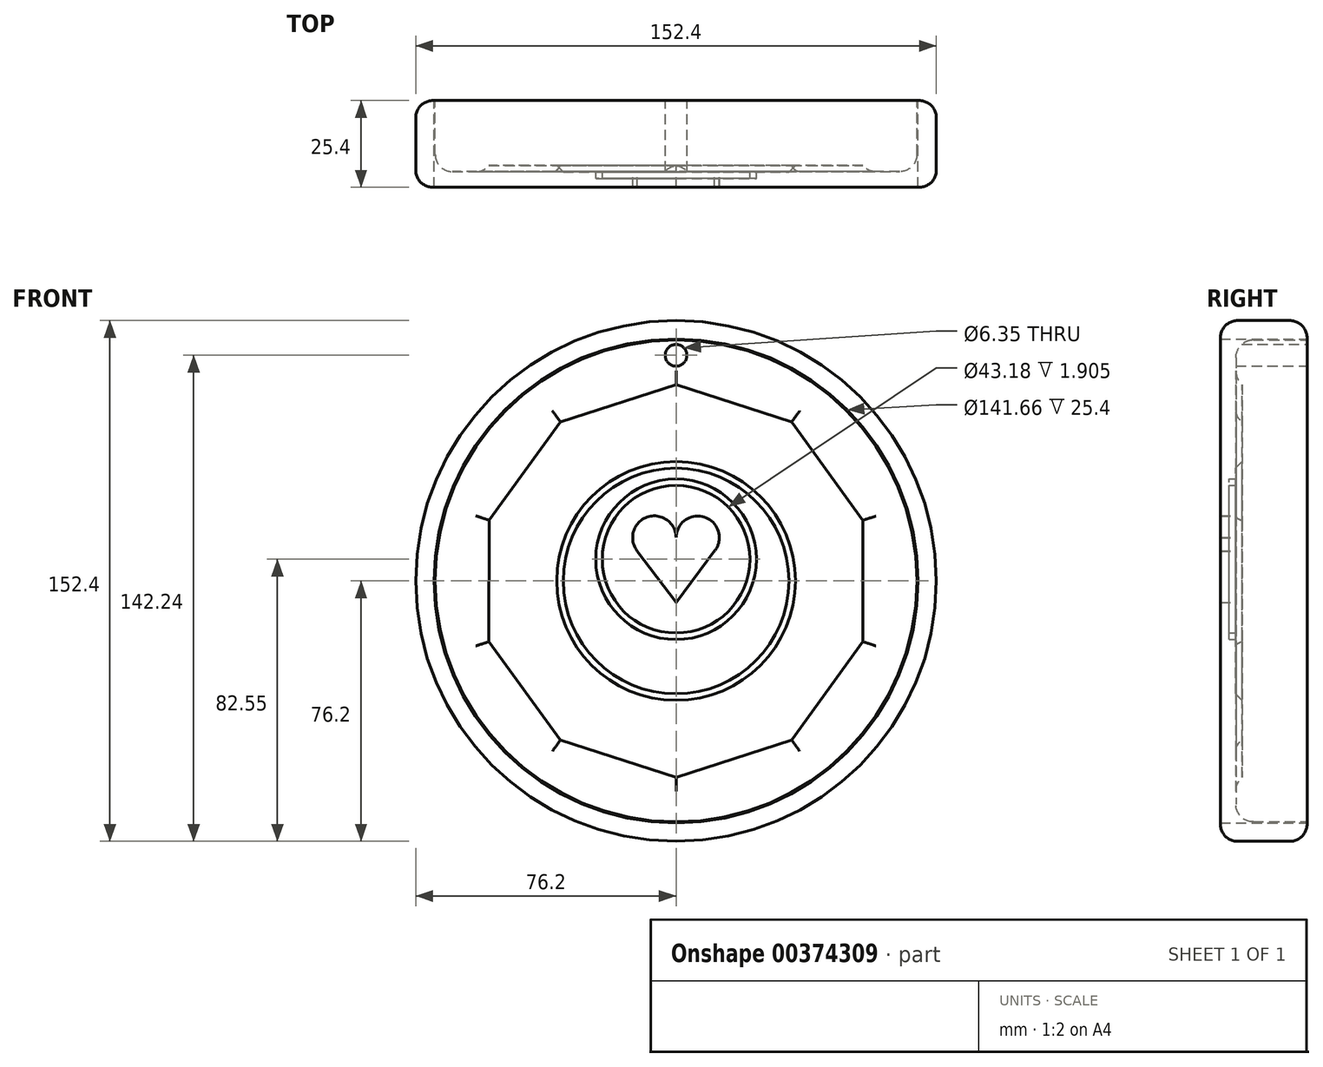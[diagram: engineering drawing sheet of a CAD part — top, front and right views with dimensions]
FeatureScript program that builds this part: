
annotation { "Feature Type Name" : "Feature", "Feature Type Description" : "" }
export const myFeature = defineFeature(function(context is Context, id is Id, definition is map)
    precondition{}
    {
        {
            var Q0;
            Q0=qCreatedBy(makeId("Front.planeOp"),FACE);
            var sketch = newSketch(context, id + "F0", { "sketchPlane" : qUnion([Q0])});
            skCircle(sketch, "E0", {"center": v(0, 0) * mm, "radius": 76.2 * mm});
            skPoint(sketch, "E1.0.midPoint", {"position": v(59.75, 28.13) * mm});
            skCircle(sketch, "E2", {"center": v(0, 0) * mm, "radius": 70.83 * mm});
            skSolve(sketch);
        }
        {
            var Q0;
            {var subQ0=sQuery(id+"F0.wireOp",EDGE,"E1.5");var subQ1=sQuery(id+"F0.wireOp",EDGE,"E0");var subQ2=makeQuery(id+"F0.imprint","INTERSECT",VERTEX,{"disambiguationData":[OD(0.0)],"derivedFrom":[subQ1,subQ0]});Q0=makeQuery(id+"F0.imprint","IMPRINT",FACE,{"disambiguationData":[TD([[makeQuery(id+"F0.imprint","IMPRINT",EDGE,{"disambiguationData":[TD([[subQ2,1.0]])],"derivedFrom":subQ1}),-1.0]])]});}
            var Q1;
            {var subQ0=sQuery(id+"F0.wireOp",EDGE,"E1.5");var subQ1=sQuery(id+"F0.wireOp",EDGE,"E0");var subQ2=makeQuery(id+"F0.imprint","INTERSECT",VERTEX,{"disambiguationData":[OD(1.0)],"derivedFrom":[subQ1,subQ0]});Q1=makeQuery(id+"F0.imprint","IMPRINT",FACE,{"disambiguationData":[TD([[makeQuery(id+"F0.imprint","IMPRINT",EDGE,{"disambiguationData":[TD([[subQ2,-1.0]])],"derivedFrom":subQ1}),-1.0]])]});}
            var Q2;
            {var subQ0=sQuery(id+"F0.wireOp",EDGE,"E1.4");var subQ1=sQuery(id+"F0.wireOp",EDGE,"E0");var subQ2=makeQuery(id+"F0.imprint","INTERSECT",VERTEX,{"disambiguationData":[OD(1.0)],"derivedFrom":[subQ1,subQ0]});Q2=makeQuery(id+"F0.imprint","IMPRINT",FACE,{"disambiguationData":[TD([[makeQuery(id+"F0.imprint","IMPRINT",EDGE,{"disambiguationData":[TD([[subQ2,-1.0]])],"derivedFrom":subQ1}),-1.0]])]});}
            var Q3;
            {var subQ0=sQuery(id+"F0.wireOp",EDGE,"E1.3");var subQ1=sQuery(id+"F0.wireOp",EDGE,"E0");var subQ2=makeQuery(id+"F0.imprint","INTERSECT",VERTEX,{"disambiguationData":[OD(1.0)],"derivedFrom":[subQ1,subQ0]});Q3=makeQuery(id+"F0.imprint","IMPRINT",FACE,{"disambiguationData":[TD([[makeQuery(id+"F0.imprint","IMPRINT",EDGE,{"disambiguationData":[TD([[subQ2,-1.0]])],"derivedFrom":subQ1}),-1.0]])]});}
            var Q4;
            {var subQ0=sQuery(id+"F0.wireOp",EDGE,"E1.2");var subQ1=sQuery(id+"F0.wireOp",EDGE,"E0");var subQ2=makeQuery(id+"F0.imprint","INTERSECT",VERTEX,{"disambiguationData":[OD(1.0)],"derivedFrom":[subQ1,subQ0]});Q4=makeQuery(id+"F0.imprint","IMPRINT",FACE,{"disambiguationData":[TD([[makeQuery(id+"F0.imprint","IMPRINT",EDGE,{"disambiguationData":[TD([[subQ2,-1.0]])],"derivedFrom":subQ1}),-1.0]])]});}
            var Q5;
            {var subQ0=sQuery(id+"F0.wireOp",EDGE,"E1.1");var subQ1=sQuery(id+"F0.wireOp",EDGE,"E0");var subQ2=makeQuery(id+"F0.imprint","INTERSECT",VERTEX,{"disambiguationData":[OD(1.0)],"derivedFrom":[subQ1,subQ0]});Q5=makeQuery(id+"F0.imprint","IMPRINT",FACE,{"disambiguationData":[TD([[makeQuery(id+"F0.imprint","IMPRINT",EDGE,{"disambiguationData":[TD([[subQ2,-1.0]])],"derivedFrom":subQ1}),-1.0]])]});}
            var Q6;
            {var subQ0=sQuery(id+"F0.wireOp",EDGE,"E1.5");var subQ1=sQuery(id+"F0.wireOp",EDGE,"E0");var subQ2=makeQuery(id+"F0.imprint","INTERSECT",VERTEX,{"disambiguationData":[OD(0.0)],"derivedFrom":[subQ1,subQ0]});Q6=makeQuery(id+"F0.imprint","IMPRINT",FACE,{"disambiguationData":[TD([[makeQuery(id+"F0.imprint","IMPRINT",EDGE,{"disambiguationData":[TD([[subQ2,-1.0]])],"derivedFrom":subQ1}),1.0]])]});}
            var Q7;
            {var subQ0=sQuery(id+"F0.wireOp",EDGE,"E1.4");var subQ1=sQuery(id+"F0.wireOp",EDGE,"E0");var subQ2=makeQuery(id+"F0.imprint","INTERSECT",VERTEX,{"disambiguationData":[OD(0.0)],"derivedFrom":[subQ1,subQ0]});Q7=makeQuery(id+"F0.imprint","IMPRINT",FACE,{"disambiguationData":[TD([[makeQuery(id+"F0.imprint","IMPRINT",EDGE,{"disambiguationData":[TD([[subQ2,-1.0]])],"derivedFrom":subQ1}),1.0]])]});}
            var Q8;
            {var subQ0=sQuery(id+"F0.wireOp",EDGE,"E1.3");var subQ1=sQuery(id+"F0.wireOp",EDGE,"E0");var subQ7=makeQuery(id+"F0.imprint","INTERSECT",VERTEX,{"disambiguationData":[OD(0.0)],"derivedFrom":[subQ1,subQ0]});Q8=makeQuery(id+"F0.imprint","IMPRINT",FACE,{"disambiguationData":[TD([[makeQuery(id+"F0.imprint","IMPRINT",EDGE,{"disambiguationData":[TD([[subQ7,-1.0]])],"derivedFrom":subQ1}),1.0]])]});}
            var Q9;
            {var subQ0=sQuery(id+"F0.wireOp",EDGE,"E1.2");var subQ1=sQuery(id+"F0.wireOp",EDGE,"E0");var subQ2=makeQuery(id+"F0.imprint","INTERSECT",VERTEX,{"disambiguationData":[OD(0.0)],"derivedFrom":[subQ1,subQ0]});Q9=makeQuery(id+"F0.imprint","IMPRINT",FACE,{"disambiguationData":[TD([[makeQuery(id+"F0.imprint","IMPRINT",EDGE,{"disambiguationData":[TD([[subQ2,-1.0]])],"derivedFrom":subQ1}),1.0]])]});}
            var Q10;
            {var subQ0=sQuery(id+"F0.wireOp",EDGE,"E1.1");var subQ1=sQuery(id+"F0.wireOp",EDGE,"E0");var subQ2=makeQuery(id+"F0.imprint","INTERSECT",VERTEX,{"disambiguationData":[OD(0.0)],"derivedFrom":[subQ1,subQ0]});Q10=makeQuery(id+"F0.imprint","IMPRINT",FACE,{"disambiguationData":[TD([[makeQuery(id+"F0.imprint","IMPRINT",EDGE,{"disambiguationData":[TD([[subQ2,-1.0]])],"derivedFrom":subQ1}),1.0]])]});}
            var Q11;
            {var subQ3=sQuery(id+"F0.wireOp",EDGE,"E1.0");var subQ5=sQuery(id+"F0.wireOp",EDGE,"E0");var subQ8=makeQuery(id+"F0.imprint","INTERSECT",VERTEX,{"disambiguationData":[OD(0.0)],"derivedFrom":[subQ5,subQ3]});Q11=makeQuery(id+"F0.imprint","IMPRINT",FACE,{"disambiguationData":[TD([[makeQuery(id+"F0.imprint","IMPRINT",EDGE,{"disambiguationData":[TD([[subQ8,1.0]])],"derivedFrom":subQ5}),1.0]])]});}
            var Q12;
            Q12=makeQuery(id+"F0.imprint","IMPRINT",FACE,{"disambiguationData":[TD([[makeQuery(id+"F0.imprint","IMPRINT",EDGE,{"derivedFrom":sQuery(id+"F0.wireOp",EDGE,"E0")}),1.0]])]});
            extrude(context, id + "F1", {"entities" : qUnion([Q0, Q1, Q2, Q3, Q4, Q5, Q6, Q7, Q8, Q9, Q10, Q11, Q12]), "depth" : 25.4 * mm});
        }
        {
            var Q0;
            Q0=makeQuery(id+"F1.opExtrude","SWEPT_FACE",FACE,{"disambiguationData":[OSD([sQuery(id+"F0.wireOp",EDGE,"E0")])]});
            fillet(context, id + "F2", {"entities" : qUnion([Q0]), "radius" : 5.08 * mm, "tangentPropagation" : true, "allowEdgeOverflow" : false});
        }
        {
            var Q0;
            Q0=qCreatedBy(makeId("Front.planeOp"),FACE);
            var sketch = newSketch(context, id + "F3", { "sketchPlane" : qUnion([Q0])});
            skCircle(sketch, "E3", {"center": v(0, 0) * mm, "radius": 70.5 * mm});
            skLineSegment(sketch, "E4.0", {"start": v(54.68, 17.76) * mm, "end": v(54.68, -17.76) * mm});
            skLineSegment(sketch, "E4.1", {"start": v(54.68, -17.76) * mm, "end": v(33.8, -46.52) * mm});
            skLineSegment(sketch, "E4.2", {"start": v(33.8, -46.52) * mm, "end": v(0, -57.49) * mm});
            skLineSegment(sketch, "E4.3", {"start": v(0, -57.49) * mm, "end": v(-33.8, -46.52) * mm});
            skLineSegment(sketch, "E4.4", {"start": v(-33.8, -46.52) * mm, "end": v(-54.8, -17.79) * mm});
            skLineSegment(sketch, "E4.5", {"start": v(-54.8, -17.79) * mm, "end": v(-54.72, 17.79) * mm});
            skLineSegment(sketch, "E4.6", {"start": v(-54.72, 17.79) * mm, "end": v(-33.85, 46.55) * mm});
            skLineSegment(sketch, "E4.7", {"start": v(-33.85, 46.55) * mm, "end": v(0, 57.49) * mm});
            skLineSegment(sketch, "E4.8", {"start": v(0, 57.49) * mm, "end": v(33.8, 46.52) * mm});
            skLineSegment(sketch, "E4.9", {"start": v(33.8, 46.52) * mm, "end": v(54.68, 17.76) * mm});
            skPoint(sketch, "E4.0.midPoint", {"position": v(54.68, 0) * mm});
            skLineSegment(sketch, "E5", {"start": v(33.8, 46.52) * mm, "end": v(41.99, 56.62) * mm});
            skLineSegment(sketch, "E6", {"start": v(54.68, 17.76) * mm, "end": v(67.2, 21.26) * mm});
            skLineSegment(sketch, "E7", {"start": v(54.68, -17.76) * mm, "end": v(66.93, -22.12) * mm});
            skLineSegment(sketch, "E8", {"start": v(33.8, -46.52) * mm, "end": v(41.86, -56.72) * mm});
            skLineSegment(sketch, "E9", {"start": v(0, -57.49) * mm, "end": v(0, -70.5) * mm});
            skLineSegment(sketch, "E10", {"start": v(0, 57.49) * mm, "end": v(0, 70.5) * mm});
            skLineSegment(sketch, "E11", {"start": v(-33.85, 46.55) * mm, "end": v(-42.66, 56.12) * mm});
            skLineSegment(sketch, "E12", {"start": v(-54.72, 17.79) * mm, "end": v(-66.63, 23.02) * mm});
            skLineSegment(sketch, "E13", {"start": v(-33.8, -46.52) * mm, "end": v(-40.82, -57.47) * mm});
            skLineSegment(sketch, "E14", {"start": v(-54.8, -17.79) * mm, "end": v(-67.63, -19.88) * mm});
            skSolve(sketch);
        }
        {
            var Q0;
            Q0 = qSketchRegion(id + "F3", true);
            extrude(context, id + "F4", {"entities" : qUnion([Q0]), "depth" : 20.83 * mm});
        }
        {
            var Q0;
            Q0=qCreatedBy(makeId("Front.planeOp"),FACE);
            var sketch = newSketch(context, id + "F5", { "sketchPlane" : qUnion([Q0])});
            skCircle(sketch, "E15", {"center": v(0, 0) * mm, "radius": 58.42 * mm});
            skSolve(sketch);
        }
        {
            var Q0;
            Q0 = qSketchRegion(id + "F5", true);
            extrude(context, id + "F6", {"entities" : qUnion([Q0]), "operationType" : NewBodyOperationType.ADD, "depth" : 19.05 * mm});
        }
        {
            var Q0;
            Q0=qCreatedBy(makeId("Front.planeOp"),FACE);
            var sketch = newSketch(context, id + "F7", { "sketchPlane" : qUnion([Q0])});
            skCircle(sketch, "E16", {"center": v(0, 0) * mm, "radius": 38.1 * mm});
            skSolve(sketch);
        }
        {
            var Q0;
            Q0 = qSketchRegion(id + "F7", true);
            extrude(context, id + "F8", {"entities" : qUnion([Q0]), "operationType" : NewBodyOperationType.ADD, "depth" : 20.95 * mm});
        }
        {
            var Q0;
            Q0=makeQuery(id+"F4.opExtrude","CAP_FACE",FACE,{"disambiguationData":[OSD([sQuery(id+"F3.wireOp",EDGE,"E3"),sQuery(id+"F3.wireOp",EDGE,"E4.0"),sQuery(id+"F3.wireOp",EDGE,"E4.1"),sQuery(id+"F3.wireOp",EDGE,"E4.2"),sQuery(id+"F3.wireOp",EDGE,"E4.3"),sQuery(id+"F3.wireOp",EDGE,"E4.4"),sQuery(id+"F3.wireOp",EDGE,"E4.5"),sQuery(id+"F3.wireOp",EDGE,"E4.6"),sQuery(id+"F3.wireOp",EDGE,"E4.7"),sQuery(id+"F3.wireOp",EDGE,"E4.8"),sQuery(id+"F3.wireOp",EDGE,"E4.9")])],"isStart":false});
            fillet(context, id + "F9", {"entities" : qUnion([Q0]), "radius" : 5.08 * mm, "tangentPropagation" : true, "allowEdgeOverflow" : false});
        }
        {
            var Q0;
            Q0=makeQuery(id+"F8.opExtrude","CAP_FACE",FACE,{"disambiguationData":[OSD([sQuery(id+"F7.wireOp",EDGE,"E16")])],"isStart":false});
            chamfer(context, id + "F10", {"entities" : qUnion([Q0]), "width" : 5.08 * mm, "tangentPropagation" : true});
        }
        {
            var Q0;
            Q0=qCreatedBy(makeId("Front.planeOp"),FACE);
            var sketch = newSketch(context, id + "F11", { "sketchPlane" : qUnion([Q0])});
            skLineSegment(sketch, "E17", {"start": v(0, 12.7) * mm, "end": v(0, 0) * mm});
            skLineSegment(sketch, "E18", {"start": v(0, 0) * mm, "end": v(0, -6.35) * mm});
            skLineSegment(sketch, "E19", {"start": v(0, 12.7) * mm, "end": v(-6.35, 12.7) * mm});
            skLineSegment(sketch, "E20", {"start": v(-6.35, 12.7) * mm, "end": v(-12.7, 12.7) * mm});
            skLineSegment(sketch, "E21", {"start": v(0, 12.7) * mm, "end": v(6.35, 12.7) * mm});
            skLineSegment(sketch, "E22", {"start": v(6.35, 12.7) * mm, "end": v(12.7, 12.7) * mm});
            skCircle(sketch, "E23", {"center": v(6.35, 12.7) * mm, "radius": 6.31 * mm});
            skCircle(sketch, "E24", {"center": v(-6.35, 12.7) * mm, "radius": 6.35 * mm});
            skLineSegment(sketch, "E25", {"start": v(0, -6.35) * mm, "end": v(-12.7, 12.7) * mm});
            skLineSegment(sketch, "E26", {"start": v(12.7, 12.7) * mm, "end": v(0, -6.35) * mm});
            skLineSegment(sketch, "E27", {"start": v(-11.31, 8.74) * mm, "end": v(0, -6.35) * mm});
            skLineSegment(sketch, "E28", {"start": v(11.28, 8.76) * mm, "end": v(0, -6.35) * mm});
            skSolve(sketch);
        }
        {
            var Q0;
            Q0 = qSketchRegion(id + "F11", true);
            extrude(context, id + "F12", {"entities" : qUnion([Q0]), "operationType" : NewBodyOperationType.ADD, "depth" : 25.4 * mm});
        }
        {
            var Q0;
            Q0=qCreatedBy(makeId("Front.planeOp"),FACE);
            var sketch = newSketch(context, id + "F13", { "sketchPlane" : qUnion([Q0])});
            skLineSegment(sketch, "E29", {"start": v(0, 0) * mm, "end": v(0, 66.04) * mm});
            skSolve(sketch);
        }
        {
            var Q0;
            Q0=sQuery(id+"F13.wireOp",VERTEX,"E29.end");
            var Q1;
            Q1=makeQuery(id+"F4.opExtrude","SWEPT_BODY",BODY,{"disambiguationData":[OSD([sQuery(id+"F3.wireOp",EDGE,"E3"),sQuery(id+"F3.wireOp",EDGE,"E4.0"),sQuery(id+"F3.wireOp",EDGE,"E4.1"),sQuery(id+"F3.wireOp",EDGE,"E4.2"),sQuery(id+"F3.wireOp",EDGE,"E4.3"),sQuery(id+"F3.wireOp",EDGE,"E4.4"),sQuery(id+"F3.wireOp",EDGE,"E4.5"),sQuery(id+"F3.wireOp",EDGE,"E4.6"),sQuery(id+"F3.wireOp",EDGE,"E4.7"),sQuery(id+"F3.wireOp",EDGE,"E4.8"),sQuery(id+"F3.wireOp",EDGE,"E4.9")])]});
            hole(context, id + "F14", {"style" : HoleStyle.SIMPLE, "endStyle" : HoleEndStyle.THROUGH, "oppositeDirection" : true, "holeDiameter" : 6.35 * mm, "isTappedThrough" : true, "tappedDepth" : 12.7 * mm, "tapClearance" : 3, "locations" : qUnion([Q0]), "scope" : qUnion([Q1])});
        }
        {
            var Q0;
            Q0=qCreatedBy(makeId("Front.planeOp"),FACE);
            var sketch = newSketch(context, id + "F15", { "sketchPlane" : qUnion([Q0])});
            skCircle(sketch, "E30", {"center": v(0, 6.35) * mm, "radius": 23.5 * mm});
            skCircle(sketch, "E31", {"center": v(0, 6.35) * mm, "radius": 21.59 * mm});
            skSolve(sketch);
        }
        {
            var Q0;
            Q0 = qSketchRegion(id + "F15", true);
            extrude(context, id + "F16", {"entities" : qUnion([Q0]), "operationType" : NewBodyOperationType.ADD, "depth" : 22.86 * mm});
        }
    });
